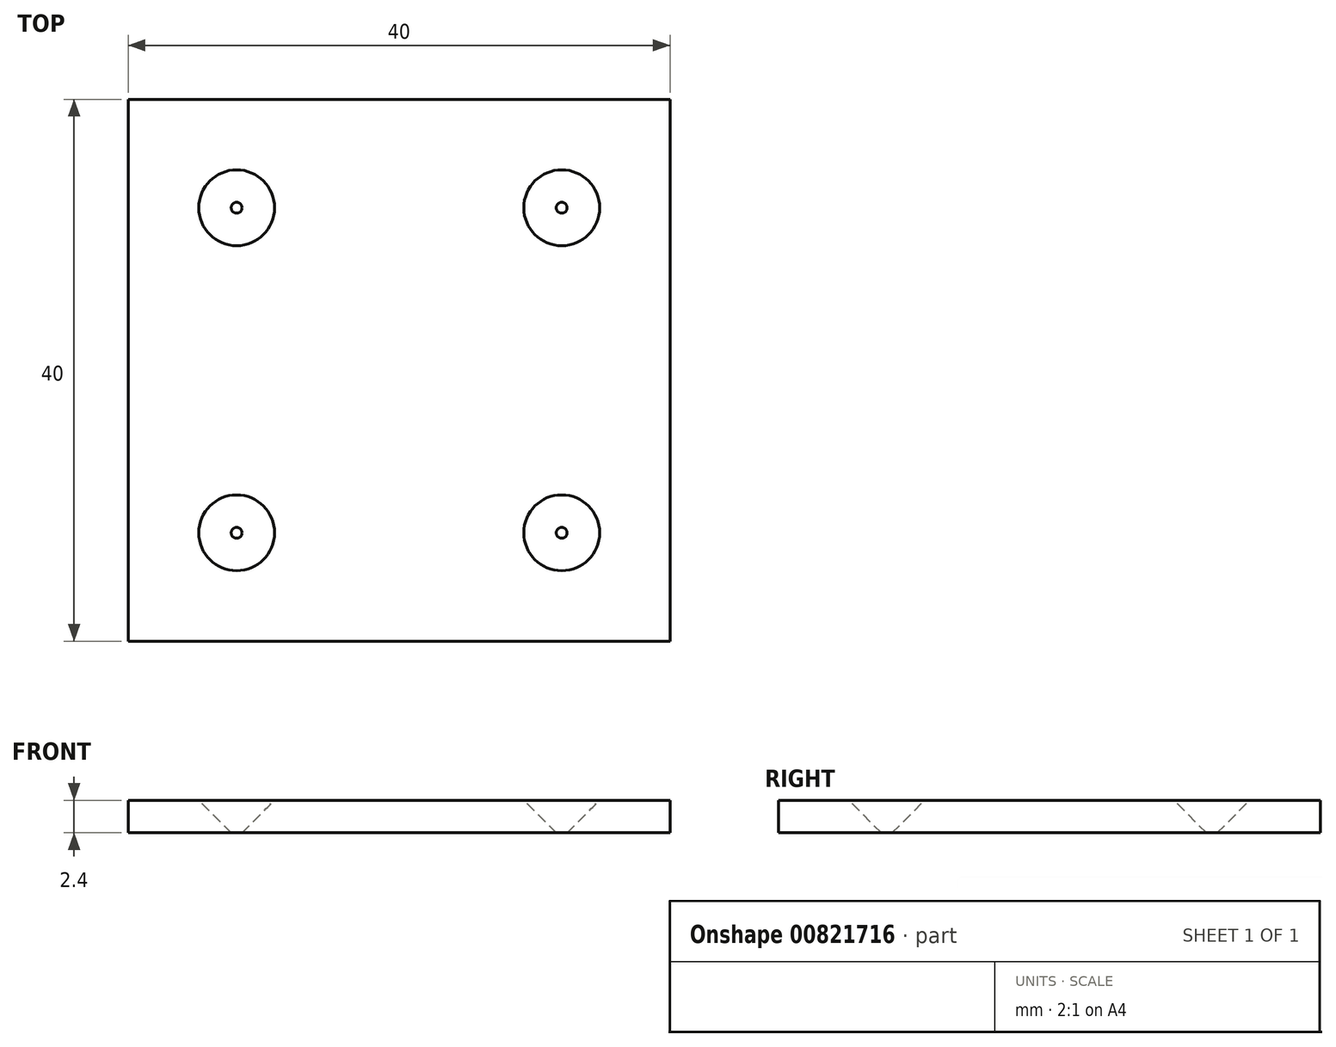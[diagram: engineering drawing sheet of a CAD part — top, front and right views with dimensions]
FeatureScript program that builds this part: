
annotation { "Feature Type Name" : "Feature", "Feature Type Description" : "" }
export const myFeature = defineFeature(function(context is Context, id is Id, definition is map)
    precondition{}
    {
        {
            var Q0;
            Q0=qCreatedBy(makeId("Top.planeOp"),FACE);
            var sketch = newSketch(context, id + "F0", { "sketchPlane" : qUnion([Q0])});
            skLineSegment(sketch, "E0.bottom", {"start": v(-20, 20) * mm, "end": v(20, 20) * mm});
            skLineSegment(sketch, "E0.top", {"start": v(-20, -20) * mm, "end": v(20, -20) * mm});
            skLineSegment(sketch, "E0.left", {"start": v(-20, 20) * mm, "end": v(-20, -20) * mm});
            skLineSegment(sketch, "E0.right", {"start": v(20, 20) * mm, "end": v(20, -20) * mm});
            skPoint(sketch, "E0.middle", {"position": v(0, 0) * mm});
            skCircle(sketch, "E1", {"center": v(-12, 12) * mm, "radius": 0.3 * mm});
            skCircle(sketch, "E2.MirrorC", {"center": v(12, 12) * mm, "radius": 0.3 * mm});
            skCircle(sketch, "E3.MirrorC", {"center": v(12, -12) * mm, "radius": 0.3 * mm});
            skCircle(sketch, "E4.MirrorC", {"center": v(-12, -12) * mm, "radius": 0.3 * mm});
            skSolve(sketch);
        }
        {
            var Q0;
            Q0=qSketchRegion(id+"F0",true);
            extrude(context, id + "F1", {"entities" : qUnion([Q0]), "depth" : 2.4 * mm, "offsetDistance" : 25 * mm});
        }
        {
            var Q0;
            Q0=makeQuery(id+"F1.opExtrude","CAP_EDGE",EDGE,{"disambiguationData":[OSD([sQuery(id+"F0.wireOp",EDGE,"E1")])],"isStart":false});
            var Q1;
            Q1=makeQuery(id+"F1.opExtrude","CAP_EDGE",EDGE,{"disambiguationData":[OSD([sQuery(id+"F0.wireOp",EDGE,"E2.MirrorC")])],"isStart":false});
            var Q2;
            Q2=makeQuery(id+"F1.opExtrude","CAP_EDGE",EDGE,{"disambiguationData":[OSD([sQuery(id+"F0.wireOp",EDGE,"E3.MirrorC")])],"isStart":false});
            var Q3;
            Q3=makeQuery(id+"F1.opExtrude","CAP_EDGE",EDGE,{"disambiguationData":[OSD([sQuery(id+"F0.wireOp",EDGE,"E4.MirrorC")])],"isStart":false});
            chamfer(context, id + "F2", {"entities" : qUnion([Q0, Q1, Q2, Q3]), "width" : 2.5 * mm, "tangentPropagation" : true});
        }
    });
